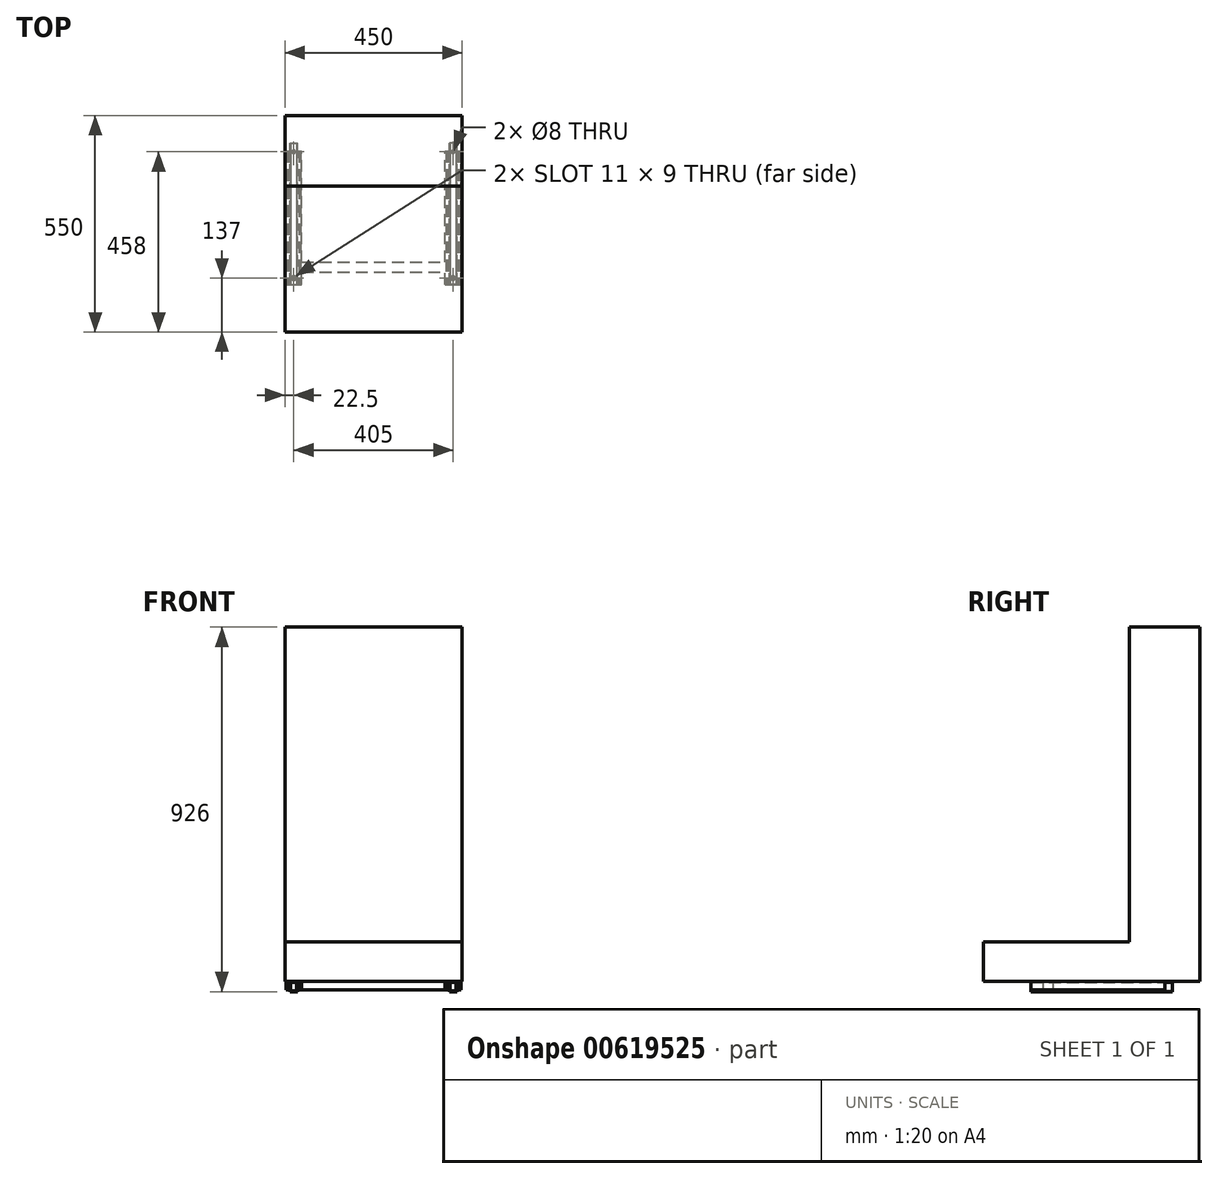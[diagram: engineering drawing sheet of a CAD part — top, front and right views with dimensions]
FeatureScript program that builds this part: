
annotation { "Feature Type Name" : "Feature", "Feature Type Description" : "" }
export const myFeature = defineFeature(function(context is Context, id is Id, definition is map)
    precondition{}
    {
        {
            var Q0;
            Q0=qCreatedBy(makeId("Right.planeOp"),FACE);
            var sketch = newSketch(context, id + "F0", { "sketchPlane" : qUnion([Q0])});
            skLineSegment(sketch, "E0.bottom", {"start": v(0, 0) * mm, "end": v(-550, 0) * mm});
            skLineSegment(sketch, "E0.top", {"start": v(0, 100) * mm, "end": v(-550, 100) * mm});
            skLineSegment(sketch, "E0.left", {"start": v(0, 0) * mm, "end": v(0, 100) * mm});
            skLineSegment(sketch, "E0.right", {"start": v(-550, 0) * mm, "end": v(-550, 100) * mm});
            skLineSegment(sketch, "E1.bottom", {"start": v(0, 100) * mm, "end": v(-179.87, 100) * mm});
            skLineSegment(sketch, "E1.top", {"start": v(0, 900) * mm, "end": v(-179.87, 900) * mm});
            skLineSegment(sketch, "E1.left", {"start": v(0, 100) * mm, "end": v(0, 900) * mm});
            skLineSegment(sketch, "E1.right", {"start": v(-179.87, 100) * mm, "end": v(-179.87, 900) * mm});
            skSolve(sketch);
        }
        {
            var Q0;
            Q0=qSketchRegion(id+"F0",true);
            extrude(context, id + "F1", {"entities" : qUnion([Q0]), "depth" : 450 * mm, "offsetDistance" : 25 * mm});
        }
        {
            var Q0;
            Q0=makeQuery(id+"F1.opExtrude","SWEPT_FACE",FACE,{"disambiguationData":[OSD([sQuery(id+"F0.wireOp",EDGE,"E0.bottom")])]});
            var sketch = newSketch(context, id + "F2", { "sketchPlane" : qUnion([Q0])});
            skLineSegment(sketch, "E2.bottom", {"start": v(2.5, 430) * mm, "end": v(42.5, 430) * mm});
            skLineSegment(sketch, "E2.top", {"start": v(2.5, 90) * mm, "end": v(42.5, 90) * mm});
            skLineSegment(sketch, "E2.left", {"start": v(2.5, 430) * mm, "end": v(2.5, 90) * mm});
            skLineSegment(sketch, "E2.right", {"start": v(42.5, 430) * mm, "end": v(42.5, 90) * mm});
            skLineSegment(sketch, "E3.bottom", {"start": v(407.5, 430) * mm, "end": v(447.5, 430) * mm});
            skLineSegment(sketch, "E3.top", {"start": v(407.5, 90) * mm, "end": v(447.5, 90) * mm});
            skLineSegment(sketch, "E3.left", {"start": v(407.5, 430) * mm, "end": v(407.5, 90) * mm});
            skLineSegment(sketch, "E3.right", {"start": v(447.5, 430) * mm, "end": v(447.5, 90) * mm});
            skLineSegment(sketch, "E4.bottom", {"start": v(42.5, 397.78) * mm, "end": v(407.5, 397.78) * mm});
            skLineSegment(sketch, "E4.top", {"start": v(42.5, 372.84) * mm, "end": v(407.5, 372.84) * mm});
            skLineSegment(sketch, "E4.left", {"start": v(42.5, 397.78) * mm, "end": v(42.5, 372.84) * mm});
            skLineSegment(sketch, "E4.right", {"start": v(407.5, 397.78) * mm, "end": v(407.5, 372.84) * mm});
            skSolve(sketch);
        }
        {
            var Q0;
            Q0=qSketchRegion(id+"F2",true);
            extrude(context, id + "F3", {"entities" : qUnion([Q0]), "depth" : 22 * mm, "offsetDistance" : 25 * mm});
        }
        {
            var Q0;
            Q0=makeQuery(id+"F3.opExtrude","SWEPT_FACE",FACE,{"disambiguationData":[OSD([sQuery(id+"F2.wireOp",EDGE,"E2.bottom")])]});
            var sketch = newSketch(context, id + "F4", { "sketchPlane" : qUnion([Q0])});
            skLineSegment(sketch, "E5.bottom", {"start": v(4.5, -2) * mm, "end": v(40.5, -2) * mm});
            skLineSegment(sketch, "E5.top", {"start": v(4.5, -20) * mm, "end": v(40.5, -20) * mm});
            skLineSegment(sketch, "E5.left", {"start": v(4.5, -2) * mm, "end": v(4.5, -20) * mm});
            skLineSegment(sketch, "E5.right", {"start": v(40.5, -2) * mm, "end": v(40.5, -20) * mm});
            skLineSegment(sketch, "E6.bottom", {"start": v(9.5, -20) * mm, "end": v(35.5, -20) * mm});
            skLineSegment(sketch, "E6.top", {"start": v(9.5, -22) * mm, "end": v(35.5, -22) * mm});
            skLineSegment(sketch, "E6.left", {"start": v(9.5, -20) * mm, "end": v(9.5, -22) * mm});
            skLineSegment(sketch, "E6.right", {"start": v(35.5, -20) * mm, "end": v(35.5, -22) * mm});
            skLineSegment(sketch, "E7.0", {"start": v(407.5, -22) * mm, "end": v(407.5, 0) * mm});
            skLineSegment(sketch, "E8.0", {"start": v(407.5, -22) * mm, "end": v(447.5, -22) * mm});
            skLineSegment(sketch, "E9.0", {"start": v(447.5, -22) * mm, "end": v(447.5, 0) * mm});
            skLineSegment(sketch, "E10.bottom", {"start": v(409.5, -2) * mm, "end": v(445.5, -2) * mm});
            skLineSegment(sketch, "E10.top", {"start": v(409.5, -20) * mm, "end": v(445.5, -20) * mm});
            skLineSegment(sketch, "E10.left", {"start": v(409.5, -2) * mm, "end": v(409.5, -20) * mm});
            skLineSegment(sketch, "E10.right", {"start": v(445.5, -2) * mm, "end": v(445.5, -20) * mm});
            skLineSegment(sketch, "E11.bottom", {"start": v(414.5, -20) * mm, "end": v(440.5, -20) * mm});
            skLineSegment(sketch, "E11.top", {"start": v(414.5, -22) * mm, "end": v(440.5, -22) * mm});
            skLineSegment(sketch, "E11.left", {"start": v(414.5, -20) * mm, "end": v(414.5, -22) * mm});
            skLineSegment(sketch, "E11.right", {"start": v(440.5, -20) * mm, "end": v(440.5, -22) * mm});
            skSolve(sketch);
        }
        {
            var Q0;
            Q0=qSketchRegion(id+"F4",true);
            extrude(context, id + "F5", {"entities" : qUnion([Q0]), "operationType" : NewBodyOperationType.REMOVE, "oppositeDirection" : true, "depth" : 372 * mm, "offsetDistance" : 25 * mm});
        }
        {
            var Q0;
            Q0=makeQuery(id+"F5.boolean.opBoolean","COPY",FACE,{"derivedFrom":makeQuery(id+"F5.opExtrude","SWEPT_FACE",FACE,{"disambiguationData":[OSD([sQuery(id+"F4.wireOp",EDGE,"E5.bottom")])]})});
            var sketch = newSketch(context, id + "F6", { "sketchPlane" : qUnion([Q0])});
            skLineSegment(sketch, "E12.bottom", {"start": v(13, 430) * mm, "end": v(32, 430) * mm});
            skLineSegment(sketch, "E12.top", {"start": v(13, 70) * mm, "end": v(32, 70) * mm});
            skLineSegment(sketch, "E12.left", {"start": v(13, 430) * mm, "end": v(13, 70) * mm});
            skLineSegment(sketch, "E12.right", {"start": v(32, 430) * mm, "end": v(32, 70) * mm});
            skLineSegment(sketch, "E13", {"start": v(225, 523.36) * mm, "end": v(225, 219) * mm, "construction": true});
            skLineSegment(sketch, "E14.MirrorCS", {"start": v(437, 70) * mm, "end": v(418, 70) * mm});
            skLineSegment(sketch, "E15.MirrorCS", {"start": v(437, 430) * mm, "end": v(418, 430) * mm});
            skLineSegment(sketch, "E16.MirrorCS", {"start": v(418, 430) * mm, "end": v(418, 70) * mm});
            skLineSegment(sketch, "E17.MirrorCS", {"start": v(437, 430) * mm, "end": v(437, 70) * mm});
            skCircle(sketch, "E18", {"center": v(22.5, 92) * mm, "radius": 4 * mm});
            skPoint(sketch, "E18.centerSnap0", {"position": v(22.5, 70) * mm});
            skLineSegment(sketch, "E19.bottom", {"start": v(18, 415.68) * mm, "end": v(27, 415.68) * mm, "construction": true});
            skLineSegment(sketch, "E19.top", {"start": v(18, 410.32) * mm, "end": v(27, 410.32) * mm, "construction": true});
            skLineSegment(sketch, "E19.left", {"start": v(18, 415.68) * mm, "end": v(18, 410.32) * mm});
            skLineSegment(sketch, "E19.right", {"start": v(27, 415.68) * mm, "end": v(27, 410.32) * mm});
            skArc(sketch, "E20", {"start": v(27, 415.68) * mm, "mid": v(22.5, 418.5) * mm, "end": v(18, 415.68) * mm});
            skArc(sketch, "E21", {"start": v(18, 410.32) * mm, "mid": v(22.5, 407.5) * mm, "end": v(27, 410.32) * mm});
            skPoint(sketch, "E22", {"position": v(22.5, 430) * mm});
            skPoint(sketch, "E23", {"position": v(18, 413) * mm});
            skCircle(sketch, "E24.MirrorC", {"center": v(427.5, 92) * mm, "radius": 4 * mm});
            skLineSegment(sketch, "E25.MirrorCS", {"start": v(432, 415.68) * mm, "end": v(432, 410.32) * mm});
            skLineSegment(sketch, "E26.MirrorCS", {"start": v(423, 415.68) * mm, "end": v(423, 410.32) * mm});
            skPoint(sketch, "E27.MirrorP", {"position": v(432, 413) * mm});
            skLineSegment(sketch, "E28.MirrorCS", {"start": v(432, 415.68) * mm, "end": v(423, 415.68) * mm, "construction": true});
            skLineSegment(sketch, "E29.MirrorCS", {"start": v(432, 410.32) * mm, "end": v(423, 410.32) * mm, "construction": true});
            skArc(sketch, "E30.MirrorCS", {"start": v(423, 415.68) * mm, "mid": v(427.5, 418.5) * mm, "end": v(432, 415.68) * mm});
            skArc(sketch, "E31.MirrorCS", {"start": v(432, 410.32) * mm, "mid": v(427.5, 407.5) * mm, "end": v(423, 410.32) * mm});
            skSolve(sketch);
        }
        {
            var Q0;
            Q0=qSketchRegion(id+"F6",true);
            extrude(context, id + "F7", {"entities" : qUnion([Q0]), "operationType" : NewBodyOperationType.ADD, "depth" : 24 * mm, "offsetDistance" : 25 * mm});
        }
        {
            var Q0;
            Q0=makeQuery(id+"F7.boolean.opBoolean","MERGE",FACE,{"derivedFrom":[makeQuery(id+"F3.opExtrude","SWEPT_FACE",FACE,{"disambiguationData":[OSD([sQuery(id+"F2.wireOp",EDGE,"E2.bottom")])]}),makeQuery(id+"F7.opExtrude","SWEPT_FACE",FACE,{"disambiguationData":[OSD([sQuery(id+"F6.wireOp",EDGE,"E12.bottom")])]})]});
            var sketch = newSketch(context, id + "F8", { "sketchPlane" : qUnion([Q0])});
            skLineSegment(sketch, "E32.bottom", {"start": v(15, -2) * mm, "end": v(30, -2) * mm});
            skLineSegment(sketch, "E32.top", {"start": v(15, -24) * mm, "end": v(30, -24) * mm});
            skLineSegment(sketch, "E32.left", {"start": v(15, -2) * mm, "end": v(15, -24) * mm});
            skLineSegment(sketch, "E32.right", {"start": v(30, -2) * mm, "end": v(30, -24) * mm});
            skLineSegment(sketch, "E33.bottom", {"start": v(420, -2) * mm, "end": v(435, -2) * mm});
            skLineSegment(sketch, "E33.top", {"start": v(420, -24) * mm, "end": v(435, -24) * mm});
            skLineSegment(sketch, "E33.left", {"start": v(420, -2) * mm, "end": v(420, -24) * mm});
            skLineSegment(sketch, "E33.right", {"start": v(435, -2) * mm, "end": v(435, -24) * mm});
            skSolve(sketch);
        }
        {
            var Q0;
            Q0=qSketchRegion(id+"F8",true);
            extrude(context, id + "F9", {"entities" : qUnion([Q0]), "operationType" : NewBodyOperationType.REMOVE, "oppositeDirection" : true, "depth" : 420 * mm, "offsetDistance" : 25 * mm});
        }
    });
